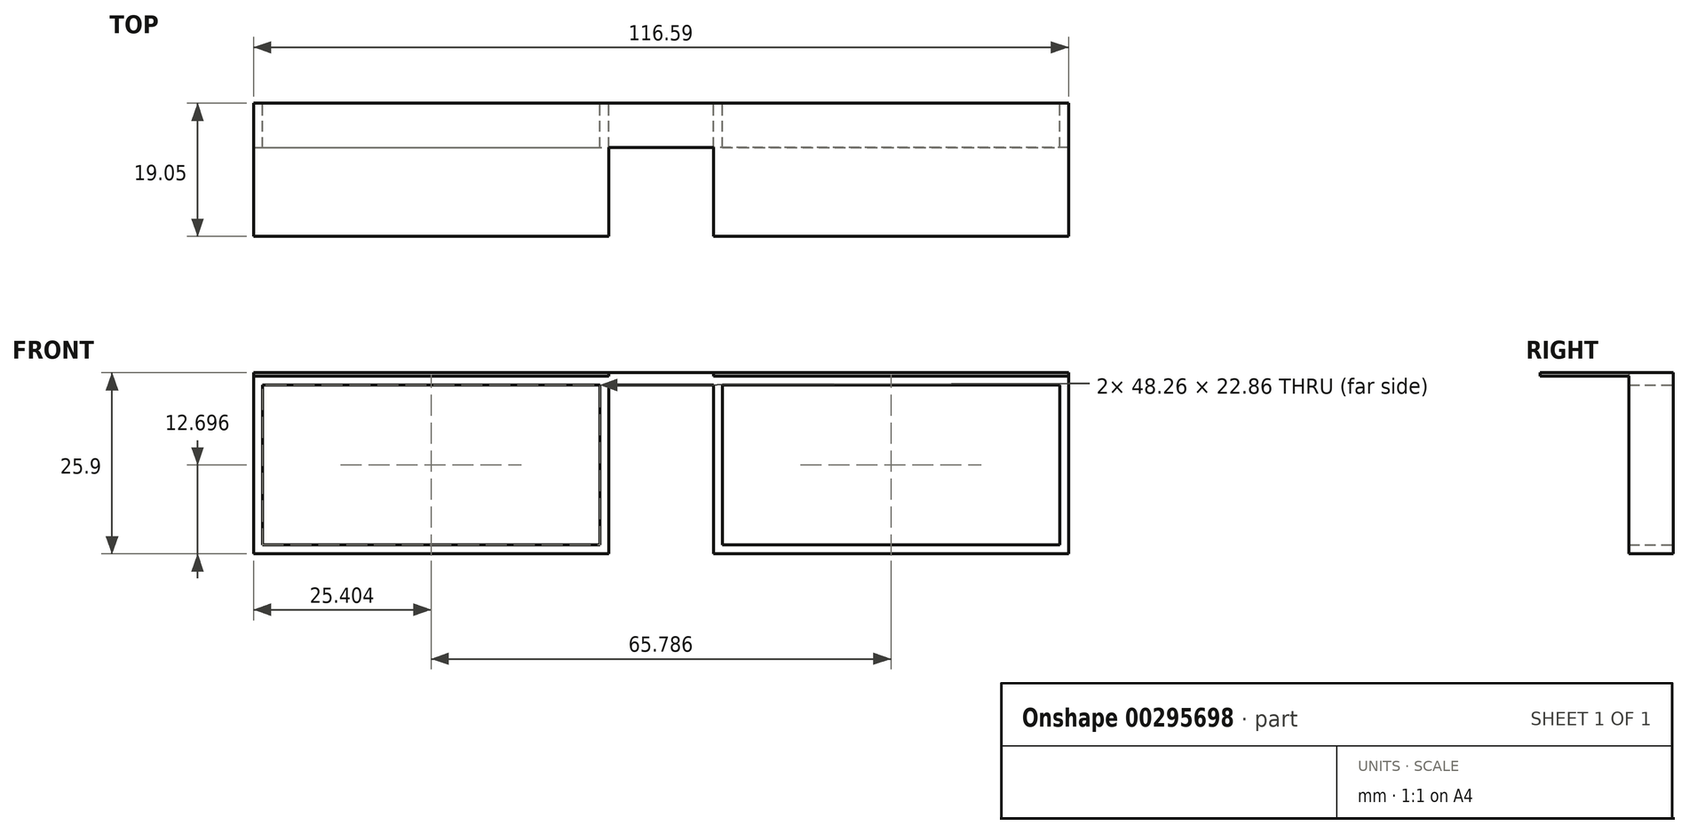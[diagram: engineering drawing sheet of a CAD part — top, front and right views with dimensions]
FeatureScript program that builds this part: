
annotation { "Feature Type Name" : "Feature", "Feature Type Description" : "" }
export const myFeature = defineFeature(function(context is Context, id is Id, definition is map)
    precondition{}
    {
        {
            var Q0;
            Q0=qCreatedBy(makeId("Front.planeOp"),FACE);
            var sketch = newSketch(context, id + "F0", { "sketchPlane" : qUnion([Q0])});
            skLineSegment(sketch, "E0", {"start": v(-65.79, 50.06) * mm, "end": v(-65.79, 24.66) * mm});
            skLineSegment(sketch, "E1", {"start": v(-14.99, 50.06) * mm, "end": v(-14.99, 34.82) * mm});
            skLineSegment(sketch, "E2", {"start": v(-65.79, 50.06) * mm, "end": v(0, 50.06) * mm});
            skLineSegment(sketch, "E3", {"start": v(-65.79, 24.66) * mm, "end": v(-14.99, 24.66) * mm});
            skLineSegment(sketch, "E4", {"start": v(0, 50.06) * mm, "end": v(0, 34.82) * mm});
            skLineSegment(sketch, "E5", {"start": v(0, 50.06) * mm, "end": v(50.8, 50.06) * mm});
            skLineSegment(sketch, "E6", {"start": v(50.8, 50.06) * mm, "end": v(50.8, 24.66) * mm});
            skLineSegment(sketch, "E7", {"start": v(50.8, 24.66) * mm, "end": v(0, 24.66) * mm});
            skLineSegment(sketch, "E8.0", {"start": v(-64.52, 48.79) * mm, "end": v(-16.26, 48.79) * mm});
            skLineSegment(sketch, "E9.0", {"start": v(-64.52, 48.79) * mm, "end": v(-64.52, 25.93) * mm});
            skLineSegment(sketch, "E10.0", {"start": v(-64.52, 25.93) * mm, "end": v(-16.26, 25.93) * mm});
            skLineSegment(sketch, "E11.0", {"start": v(-16.26, 48.79) * mm, "end": v(-16.26, 25.93) * mm});
            skLineSegment(sketch, "E12.0", {"start": v(1.27, 48.79) * mm, "end": v(49.53, 48.79) * mm});
            skLineSegment(sketch, "E13.0", {"start": v(1.27, 48.79) * mm, "end": v(1.27, 25.93) * mm});
            skLineSegment(sketch, "E14.0", {"start": v(49.53, 25.93) * mm, "end": v(1.27, 25.93) * mm});
            skLineSegment(sketch, "E15.0", {"start": v(49.53, 48.79) * mm, "end": v(49.53, 25.93) * mm});
            skLineSegment(sketch, "E16.trimOffspring", {"start": v(-14.99, 34.82) * mm, "end": v(-14.99, 24.66) * mm});
            skLineSegment(sketch, "E17.trimOffspring", {"start": v(0, 34.82) * mm, "end": v(0, 24.66) * mm});
            skLineSegment(sketch, "E18.trimOffspring", {"start": v(-14.99, 48.79) * mm, "end": v(0, 48.79) * mm});
            skSolve(sketch);
        }
        {
            var Q0;
            {var subQ3=sQuery(id+"F0.wireOp",EDGE,"E18.trimOffspring");Q0=makeQuery(id+"F0.imprint","IMPRINT",FACE,{"disambiguationData":[TD([[makeQuery(id+"F0.imprint","IMPRINT",EDGE,{"derivedFrom":subQ3}),1.0]])]});}
            extrude(context, id + "F1", {"entities" : qUnion([Q0]), "depth" : 1.27 * mm});
        }
        {
            var Q0;
            Q0 = qSketchRegion(id + "F0", true);
            extrude(context, id + "F2", {"entities" : qUnion([Q0]), "operationType" : NewBodyOperationType.ADD, "depth" : 6.35 * mm});
        }
        {
            var Q0;
            {var subQ0=sQuery(id+"F0.wireOp",EDGE,"E2");Q0=makeQuery(id+"F2.boolean.opBoolean","MERGE",FACE,{"derivedFrom":[makeQuery(id+"F1.opExtrude","SWEPT_FACE",FACE,{"disambiguationData":[OSD([subQ0])]}),makeQuery(id+"F2.opExtrude","SWEPT_FACE",FACE,{"disambiguationData":[OSD([subQ0,sQuery(id+"F0.wireOp",EDGE,"E5")])]})]});}
            var sketch = newSketch(context, id + "F3", { "sketchPlane" : qUnion([Q0])});
            skPoint(sketch, "E19", {"position": v(-7.5, -6.35) * mm});
            skLineSegment(sketch, "E20", {"start": v(-65.79, -6.35) * mm, "end": v(-65.79, -19.05) * mm});
            skLineSegment(sketch, "E21", {"start": v(-65.79, -19.05) * mm, "end": v(-14.99, -19.05) * mm});
            skLineSegment(sketch, "E22", {"start": v(-14.99, -19.05) * mm, "end": v(-14.99, -6.35) * mm});
            skLineSegment(sketch, "E23", {"start": v(0, -6.35) * mm, "end": v(0, -19.05) * mm});
            skLineSegment(sketch, "E24", {"start": v(0, -19.05) * mm, "end": v(50.8, -19.05) * mm});
            skLineSegment(sketch, "E25", {"start": v(50.8, -19.05) * mm, "end": v(50.8, -6.35) * mm});
            skSolve(sketch);
        }
        {
            var Q0;
            {var subQ0=sQuery(id+"F3.wireOp",EDGE,"0qIjOkoI-qbUD-5mID-GXbc-gNCGJZyRe2uQ");Q0=makeQuery(id+"F3.imprint","IMPRINT",FACE,{"disambiguationData":[TD([[makeQuery(id+"F3.imprint","IMPRINT",EDGE,{"derivedFrom":subQ0}),1.0]])]});}
            var Q1;
            {var subQ0=sQuery(id+"F3.wireOp",EDGE,"aQi7KkJF-eABa-9AEJ-TGBJ-Z5ciBShmPf9Q");Q1=makeQuery(id+"F3.imprint","IMPRINT",FACE,{"disambiguationData":[TD([[makeQuery(id+"F3.imprint","IMPRINT",EDGE,{"derivedFrom":subQ0}),1.0]])]});}
            var Q2;
            {var subQ0=sQuery(id+"F3.wireOp",EDGE,"E20");Q2=makeQuery(id+"F3.imprint","IMPRINT",FACE,{"disambiguationData":[TD([[makeQuery(id+"F3.imprint","IMPRINT",EDGE,{"derivedFrom":subQ0}),1.0]])]});}
            var Q3;
            {var subQ0=sQuery(id+"F3.wireOp",EDGE,"E23");Q3=makeQuery(id+"F3.imprint","IMPRINT",FACE,{"disambiguationData":[TD([[makeQuery(id+"F3.imprint","IMPRINT",EDGE,{"derivedFrom":subQ0}),1.0]])]});}
            var Q4;
            {var subQ1=sQuery(id+"F0.wireOp",EDGE,"E2");var subQ6=makeQuery(id+"F2.opExtrude","SWEPT_EDGE",EDGE,{"disambiguationData":[OSD([sQuery(id+"F0.wireOp",EDGE,"E0"),subQ1])]});Q4=makeQuery(id+"F3.imprint","IMPRINT",FACE,{"disambiguationData":[TD([[makeQuery(id+"F3.imprint","IMPRINT",EDGE,{"derivedFrom":subQ6}),-1.0]])]});}
            extrude(context, id + "F4", {"entities" : qUnion([Q0, Q1, Q2, Q3, Q4]), "operationType" : NewBodyOperationType.ADD, "depth" : 0.5 * mm});
        }
    });
